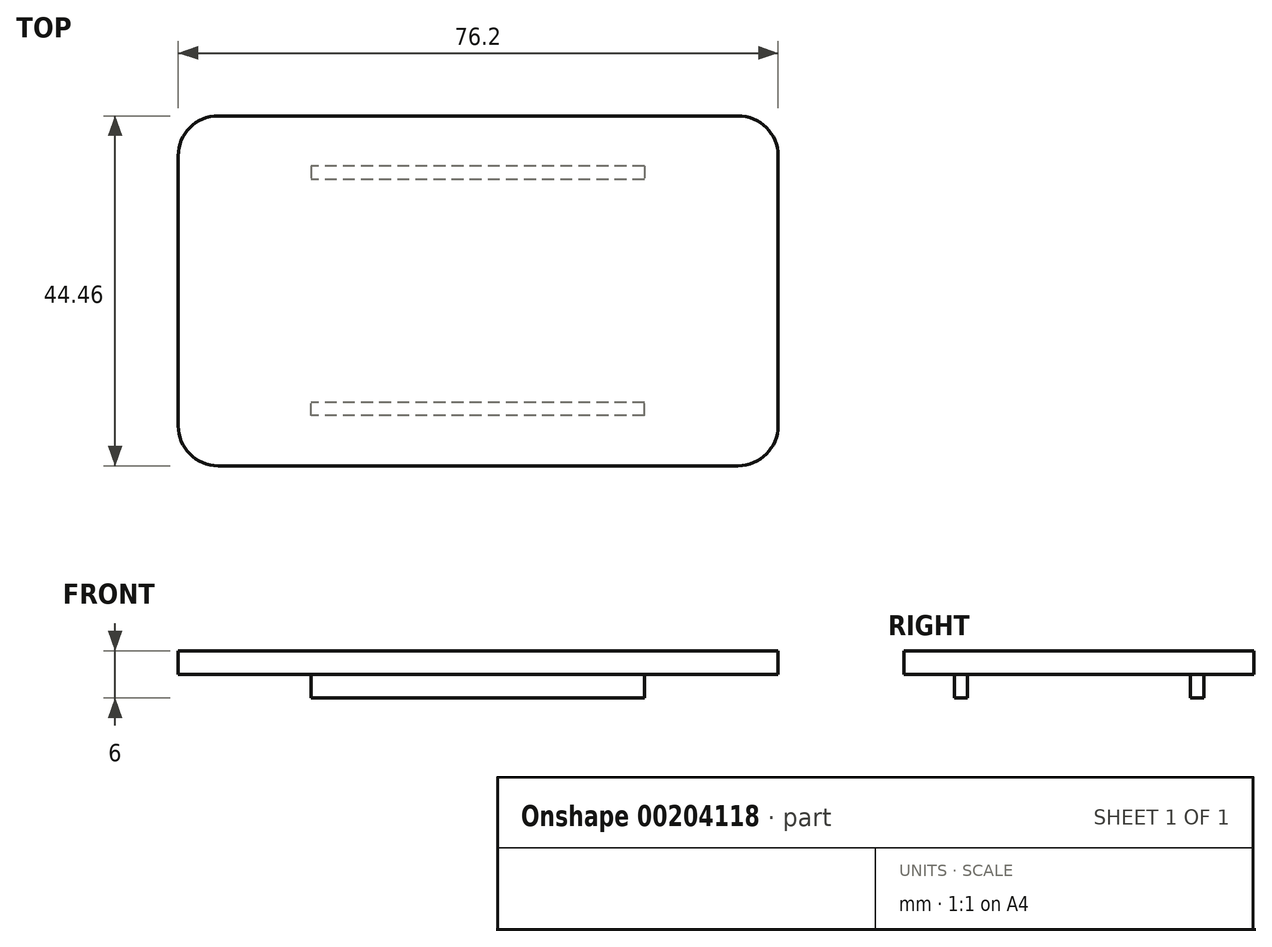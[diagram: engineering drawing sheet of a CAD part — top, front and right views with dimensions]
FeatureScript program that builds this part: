
annotation { "Feature Type Name" : "Feature", "Feature Type Description" : "" }
export const myFeature = defineFeature(function(context is Context, id is Id, definition is map)
    precondition{}
    {
        {
            var Q0;
            Q0=qCreatedBy(makeId("Top.planeOp"),FACE);
            var sketch = newSketch(context, id + "F0", { "sketchPlane" : qUnion([Q0])});
            skLineSegment(sketch, "E0.bottom", {"start": v(38.1, 22.22) * mm, "end": v(-38.1, 22.22) * mm});
            skLineSegment(sketch, "E0.top", {"start": v(38.1, -22.22) * mm, "end": v(-38.1, -22.22) * mm});
            skLineSegment(sketch, "E0.left", {"start": v(38.1, 22.22) * mm, "end": v(38.1, -22.22) * mm});
            skLineSegment(sketch, "E0.right", {"start": v(-38.1, 22.22) * mm, "end": v(-38.1, -22.23) * mm});
            skPoint(sketch, "E0.middle", {"position": v(0, 0) * mm});
            skLineSegment(sketch, "E1", {"start": v(-27.37, 9.9) * mm, "end": v(-27.37, -10.03) * mm});
            skCircle(sketch, "E2", {"center": v(-27.37, 9.9) * mm, "radius": 5.5 * mm});
            skCircle(sketch, "E3", {"center": v(-27.37, -10.03) * mm, "radius": 5.5 * mm});
            skLineSegment(sketch, "E4", {"start": v(-25.66, 4.67) * mm, "end": v(-25.66, -4.8) * mm});
            skLineSegment(sketch, "E5", {"start": v(-30.05, 5.1) * mm, "end": v(-30.05, -5.23) * mm});
            skLineSegment(sketch, "E6", {"start": v(-25.66, 1.93) * mm, "end": v(26.37, 1.93) * mm});
            skLineSegment(sketch, "E7", {"start": v(-25.66, -2) * mm, "end": v(26.37, -2) * mm});
            skLineSegment(sketch, "E8", {"start": v(26.37, -2) * mm, "end": v(28.74, -2) * mm});
            skLineSegment(sketch, "E9", {"start": v(26.37, 1.93) * mm, "end": v(28.74, 1.93) * mm});
            skLineSegment(sketch, "E10", {"start": v(28.74, -2) * mm, "end": v(28.74, 1.93) * mm});
            skPoint(sketch, "E10.endSnap0", {"position": v(28.08, 1.93) * mm});
            skPoint(sketch, "E11.orphan", {"position": v(29.8, 1.93) * mm});
            skSolve(sketch);
        }
        {
            var Q0;
            Q0=makeQuery(id+"F0.imprint","IMPRINT",FACE,{"disambiguationData":[TD([[makeQuery(id+"F0.imprint","IMPRINT",EDGE,{"derivedFrom":sQuery(id+"F0.wireOp",EDGE,"E0.bottom")}),1.0]])]});
            extrude(context, id + "F1", {"entities" : qUnion([Q0]), "depth" : 3 * mm});
        }
        {
            var Q0;
            {var subQ1=sQuery(id+"F0.wireOp",EDGE,"E6");Q0=makeQuery(id+"F0.imprint","IMPRINT",FACE,{"disambiguationData":[TD([[makeQuery(id+"F0.imprint","IMPRINT",EDGE,{"derivedFrom":subQ1}),-1.0]])]});}
            var Q1;
            {var subQ0=sQuery(id+"F0.wireOp",EDGE,"E3");var subQ1=makeQuery(id+"F0.imprint","INTERSECT",VERTEX,{"derivedFrom":[subQ0,sQuery(id+"F0.wireOp",EDGE,"E4")]});Q1=makeQuery(id+"F0.imprint","IMPRINT",FACE,{"disambiguationData":[TD([[makeQuery(id+"F0.imprint","IMPRINT",EDGE,{"disambiguationData":[TD([[subQ1,-1.0]])],"derivedFrom":subQ0}),1.0]])]});}
            var Q2;
            {var subQ5=sQuery(id+"F0.wireOp",EDGE,"E5");Q2=makeQuery(id+"F0.imprint","IMPRINT",FACE,{"disambiguationData":[TD([[makeQuery(id+"F0.imprint","IMPRINT",EDGE,{"derivedFrom":subQ5}),1.0]])]});}
            var Q3;
            {var subQ0=sQuery(id+"F0.wireOp",EDGE,"E2");var subQ1=makeQuery(id+"F0.imprint","INTERSECT",VERTEX,{"derivedFrom":[subQ0,sQuery(id+"F0.wireOp",EDGE,"E5")]});Q3=makeQuery(id+"F0.imprint","IMPRINT",FACE,{"disambiguationData":[TD([[makeQuery(id+"F0.imprint","IMPRINT",EDGE,{"disambiguationData":[TD([[subQ1,-1.0]])],"derivedFrom":subQ0}),1.0]])]});}
            var Q4;
            {var subQ1=sQuery(id+"F0.wireOp",EDGE,"E2");var subQ6=sQuery(id+"F0.wireOp",EDGE,"E1");var subQ8=makeQuery(id+"F0.imprint","INTERSECT",VERTEX,{"derivedFrom":[subQ6,subQ1]});Q4=makeQuery(id+"F0.imprint","IMPRINT",FACE,{"disambiguationData":[TD([[makeQuery(id+"F0.imprint","IMPRINT",EDGE,{"disambiguationData":[TD([[subQ8,-1.0]])],"derivedFrom":subQ6}),1.0]])]});}
            extrude(context, id + "F2", {"entities" : qUnion([Q0, Q1, Q2, Q3, Q4]), "operationType" : NewBodyOperationType.ADD, "depth" : 3 * mm});
        }
        {
            var Q0;
            Q0=makeQuery(id+"F1.opExtrude","SWEPT_EDGE",EDGE,{"disambiguationData":[OSD([sQuery(id+"F0.wireOp",EDGE,"E0.bottom"),sQuery(id+"F0.wireOp",EDGE,"E0.left")])]});
            var Q1;
            Q1=makeQuery(id+"F1.opExtrude","SWEPT_EDGE",EDGE,{"disambiguationData":[OSD([sQuery(id+"F0.wireOp",EDGE,"E0.top"),sQuery(id+"F0.wireOp",EDGE,"E0.left")])]});
            var Q2;
            Q2=makeQuery(id+"F1.opExtrude","SWEPT_EDGE",EDGE,{"disambiguationData":[OSD([sQuery(id+"F0.wireOp",EDGE,"E0.top"),sQuery(id+"F0.wireOp",EDGE,"E0.right")])]});
            var Q3;
            Q3=makeQuery(id+"F1.opExtrude","SWEPT_EDGE",EDGE,{"disambiguationData":[OSD([sQuery(id+"F0.wireOp",EDGE,"E0.bottom"),sQuery(id+"F0.wireOp",EDGE,"E0.right")])]});
            fillet(context, id + "F3", {"entities" : qUnion([Q0, Q1, Q2, Q3]), "radius" : 5.08 * mm, "tangentPropagation" : true, "allowEdgeOverflow" : false});
        }
        {
            var Q0;
            Q0=makeQuery(id+"F0.imprint","IMPRINT",FACE,{"disambiguationData":[TD([[makeQuery(id+"F0.imprint","IMPRINT",EDGE,{"derivedFrom":sQuery(id+"F0.wireOp",EDGE,"E0.bottom")}),1.0]])]});
            var sketch = newSketch(context, id + "F4", { "sketchPlane" : qUnion([Q0])});
            skLineSegment(sketch, "E12.bottom", {"start": v(21.14, -15.83) * mm, "end": v(-21.22, -15.83) * mm});
            skLineSegment(sketch, "E12.top", {"start": v(21.14, -14.16) * mm, "end": v(-21.22, -14.16) * mm});
            skLineSegment(sketch, "E12.left", {"start": v(21.14, -15.83) * mm, "end": v(21.14, -14.16) * mm});
            skLineSegment(sketch, "E12.right", {"start": v(-21.22, -15.83) * mm, "end": v(-21.22, -14.16) * mm});
            skLineSegment(sketch, "E13.MirrorCS", {"start": v(21.14, 14.16) * mm, "end": v(-21.22, 14.16) * mm});
            skLineSegment(sketch, "E14.MirrorCS", {"start": v(21.14, 15.83) * mm, "end": v(-21.22, 15.83) * mm});
            skLineSegment(sketch, "E15.MirrorCS", {"start": v(21.14, 15.83) * mm, "end": v(21.14, 14.16) * mm});
            skLineSegment(sketch, "E16.MirrorCS", {"start": v(-21.22, 15.83) * mm, "end": v(-21.22, 14.16) * mm});
            skSolve(sketch);
        }
        {
            var Q0;
            Q0=makeQuery(id+"F4.imprint","IMPRINT",FACE,{"disambiguationData":[TD([[makeQuery(id+"F4.imprint","IMPRINT",EDGE,{"derivedFrom":sQuery(id+"F4.wireOp",EDGE,"E12.bottom")}),-1.0]])]});
            var Q1;
            Q1=makeQuery(id+"F4.imprint","IMPRINT",FACE,{"disambiguationData":[TD([[makeQuery(id+"F4.imprint","IMPRINT",EDGE,{"derivedFrom":sQuery(id+"F4.wireOp",EDGE,"E13.MirrorCS")}),-1.0]])]});
            extrude(context, id + "F5", {"entities" : qUnion([Q0, Q1]), "operationType" : NewBodyOperationType.ADD, "oppositeDirection" : true, "depth" : 3 * mm});
        }
    });
